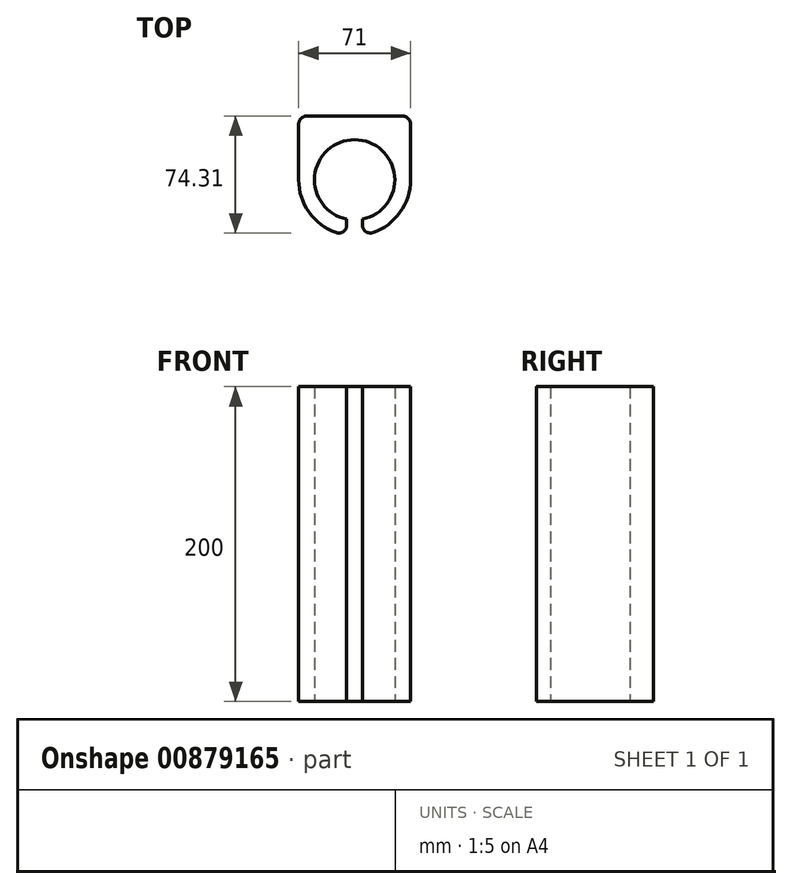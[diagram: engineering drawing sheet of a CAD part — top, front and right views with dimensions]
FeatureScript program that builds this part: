
annotation { "Feature Type Name" : "Feature", "Feature Type Description" : "" }
export const myFeature = defineFeature(function(context is Context, id is Id, definition is map)
    precondition{}
    {
        {
            var Q0;
            Q0=qCreatedBy(makeId("Top.planeOp"),FACE);
            var sketch = newSketch(context, id + "F0", { "sketchPlane" : qUnion([Q0])});
            skArc(sketch, "E0", {"start": v(5, -25) * mm, "mid": v(0, 25.5) * mm, "end": v(-5, -25) * mm});
            skArc(sketch, "E1", {"start": v(5, -35.15) * mm, "mid": v(26.81, -23.27) * mm, "end": v(35.5, 0) * mm});
            skLineSegment(sketch, "E2", {"start": v(-5, -25) * mm, "end": v(-5, -35.15) * mm});
            skLineSegment(sketch, "E3", {"start": v(5, -25) * mm, "end": v(5, -35.15) * mm});
            skLineSegment(sketch, "E4", {"start": v(0, 35.5) * mm, "end": v(-35.5, 35.5) * mm});
            skLineSegment(sketch, "E5", {"start": v(39.9, 0) * mm, "end": v(25.5, 0) * mm, "construction": true});
            skLineSegment(sketch, "E6", {"start": v(-35.5, 0) * mm, "end": v(-35.5, 35.5) * mm});
            skLineSegment(sketch, "E7", {"start": v(0, 35.5) * mm, "end": v(35.5, 35.5) * mm});
            skLineSegment(sketch, "E8", {"start": v(35.5, 0) * mm, "end": v(35.5, 35.5) * mm});
            skArc(sketch, "E9.trimOffspring", {"start": v(-35.5, 0) * mm, "mid": v(-26.81, -23.27) * mm, "end": v(-5, -35.15) * mm});
            skSolve(sketch);
        }
        {
            var Q0;
            Q0 = qSketchRegion(id + "F0", true);
            extrude(context, id + "F1", {"entities" : qUnion([Q0]), "depth" : 200 * mm, "offsetDistance" : 25 * mm});
        }
        {
            var Q0;
            Q0=makeQuery(id+"F1.opExtrude","SWEPT_EDGE",EDGE,{"disambiguationData":[OSD([sQuery(id+"F0.wireOp",EDGE,"E2"),sQuery(id+"F0.wireOp",EDGE,"E9.trimOffspring")])]});
            var Q1;
            Q1=makeQuery(id+"F1.opExtrude","SWEPT_EDGE",EDGE,{"disambiguationData":[OSD([sQuery(id+"F0.wireOp",EDGE,"E1"),sQuery(id+"F0.wireOp",EDGE,"E3")])]});
            fillet(context, id + "F2", {"entities" : qUnion([Q0, Q1]), "radius" : 5 * mm, "tangentPropagation" : true, "allowEdgeOverflow" : false});
        }
        {
            var Q0;
            Q0=makeQuery(id+"F1.opExtrude","SWEPT_FACE",FACE,{"disambiguationData":[OSD([sQuery(id+"F0.wireOp",EDGE,"E4"),sQuery(id+"F0.wireOp",EDGE,"E7")])]});
            extrude(context, id + "F3", {"entities" : qUnion([Q0]), "operationType" : NewBodyOperationType.ADD, "depth" : 5 * mm, "offsetDistance" : 25 * mm});
        }
        {
            var Q0;
            Q0=makeQuery(id+"F3.opExtrude","CAP_EDGE",EDGE,{"disambiguationData":[OSD([sQuery(id+"F0.wireOp",EDGE,"E7"),sQuery(id+"F0.wireOp",EDGE,"E8")])],"isStart":false});
            var Q1;
            Q1=makeQuery(id+"F3.opExtrude","CAP_EDGE",EDGE,{"disambiguationData":[OSD([sQuery(id+"F0.wireOp",EDGE,"E4"),sQuery(id+"F0.wireOp",EDGE,"E6")])],"isStart":false});
            fillet(context, id + "F4", {"entities" : qUnion([Q0, Q1]), "radius" : 5 * mm, "tangentPropagation" : true, "allowEdgeOverflow" : false});
        }
    });
